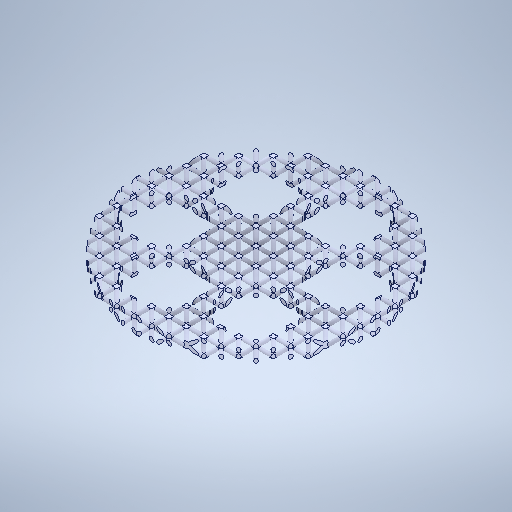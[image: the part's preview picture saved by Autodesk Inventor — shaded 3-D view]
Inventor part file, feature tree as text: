
AUTODESK INVENTOR PART (.ipt)
format: ipt  version: 2025.3 (Build 293356000, 356)  size: 4,054,016 bytes
history: native  units: in
note: dims shown in document units (in); Inventor stores cm internally (conversion verified against a paired STEP export)
features: extrude x2, sketch x2, projected_geometry x2, pattern_linear x1, plane x1, other x1
ambient origin geometry x8: Origin, YZ Plane, XZ Plane, XY Plane, X Axis, Y Axis, Z Axis, Center Point
bodies: Solid1 (feature_tree)
feature tree (9):
  pattern_linear  "Rectangular Pattern1"  Count1=14 Spacing1=0.315in
  plane  "Work Plane1"
  extrude  "Extrusion1"  Depth=2.3622in
  extrude  "Extrusion3"  Depth=1.1811in
  sketch  "Sketch1"  dims[d6=4.3307in d7=2.3622in]
  sketch  "Sketch2"  dims[d8=1.1811in d9=1.1811in d10=1.1811in d11=1.1811in d12=1.1811in d13=1.1811in d14=4.3307in d15=0.0in d16=4.3307in d19=4.3307in d20=0.0in d17=0.0197in d18=1.9685in]
  other  "Cut-Extrude14"
  projected_geometry  "Project Cut Edges1"
  projected_geometry  "Project Cut Edges2"
